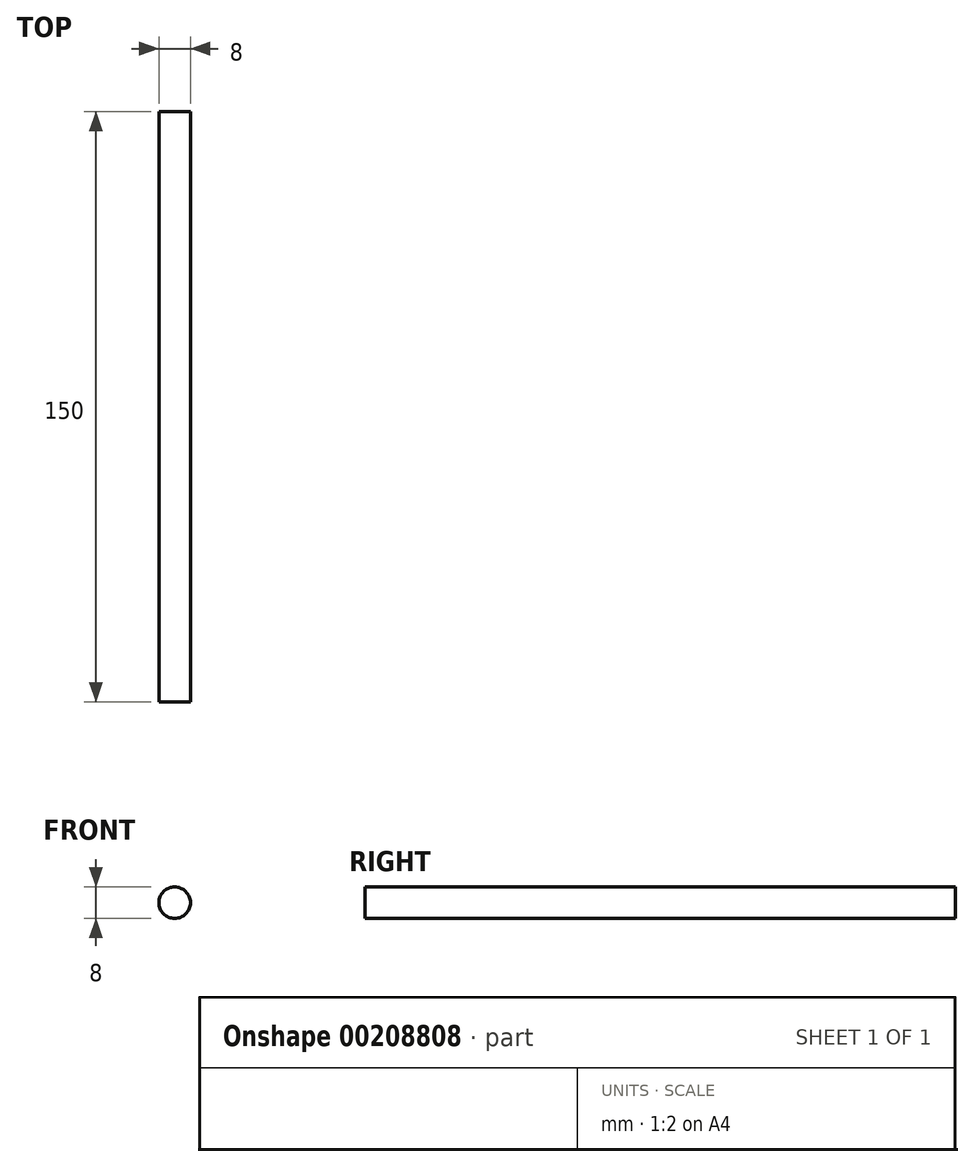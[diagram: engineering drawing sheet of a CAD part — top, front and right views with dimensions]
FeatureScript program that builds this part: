
annotation { "Feature Type Name" : "Feature", "Feature Type Description" : "" }
export const myFeature = defineFeature(function(context is Context, id is Id, definition is map)
    precondition{}
    {
        {
            var Q0;
            Q0=qCreatedBy(makeId("Front.planeOp"),FACE);
            var sketch = newSketch(context, id + "F0", { "sketchPlane" : qUnion([Q0])});
            skCircle(sketch, "E0", {"center": v(0, 0) * mm, "radius": 4 * mm});
            skSolve(sketch);
        }
        {
            var Q0;
            Q0=qSketchRegion(id+"F0",true);
            extrude(context, id + "F1", {"entities" : qUnion([Q0]), "depth" : 150 * mm});
        }
    });
